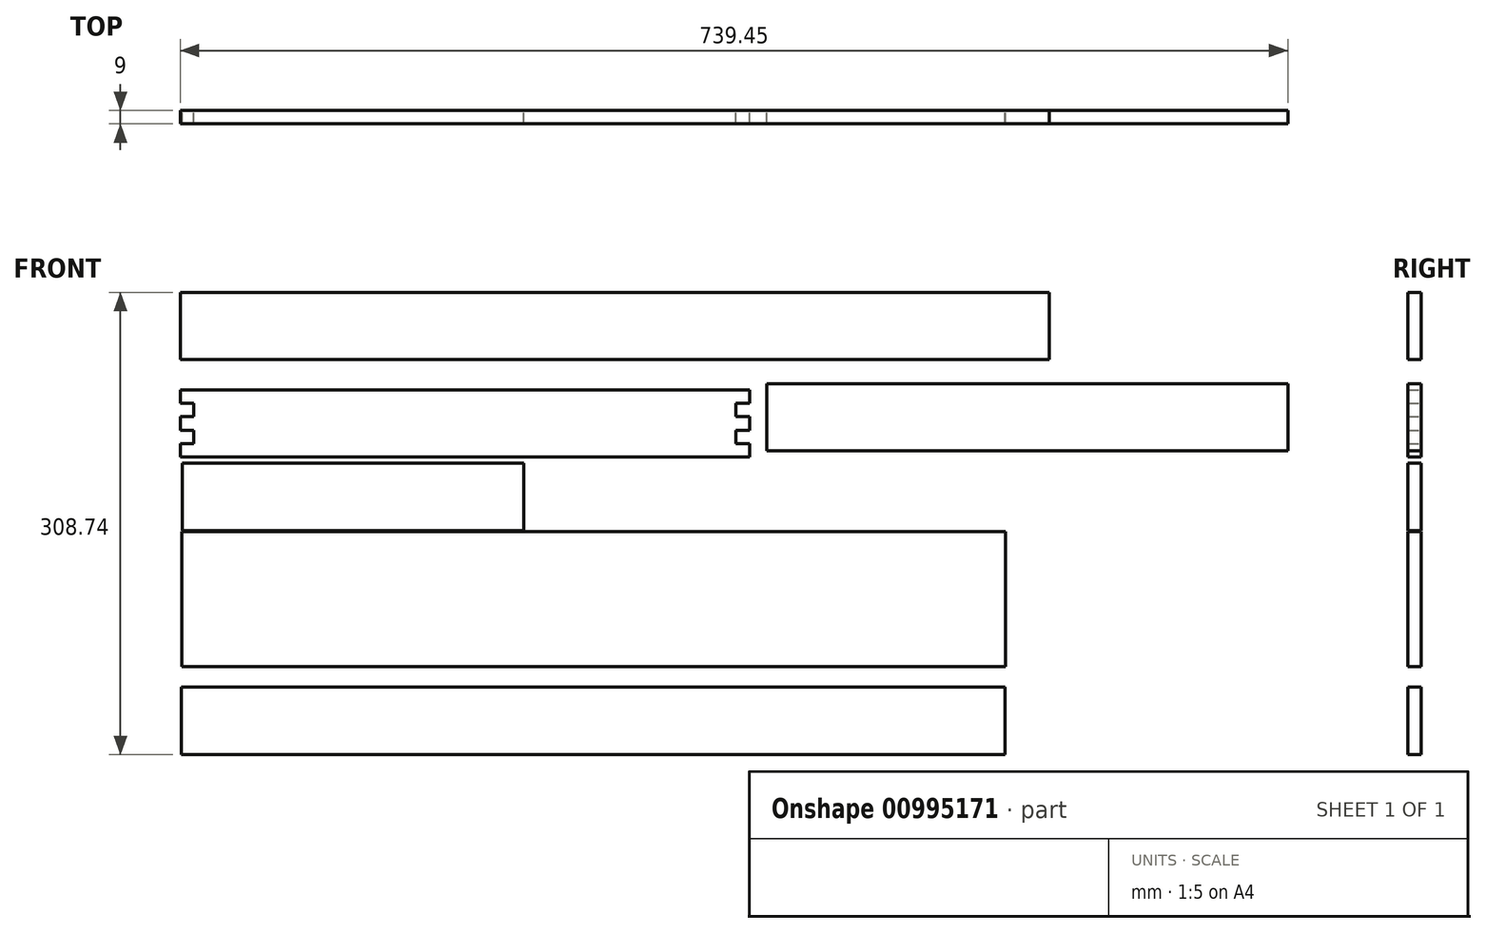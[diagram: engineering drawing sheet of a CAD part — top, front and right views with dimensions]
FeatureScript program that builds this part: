
annotation { "Feature Type Name" : "Feature", "Feature Type Description" : "" }
export const myFeature = defineFeature(function(context is Context, id is Id, definition is map)
    precondition{}
    {
        {
            var Q0;
            Q0=qCreatedBy(makeId("Front.planeOp"),FACE);
            var sketch = newSketch(context, id + "F0", { "sketchPlane" : qUnion([Q0])});
            skLineSegment(sketch, "E0.bottom", {"start": v(-581.65, 301.64) * mm, "end": v(-1.65, 301.64) * mm});
            skLineSegment(sketch, "E0.top", {"start": v(-581.65, 256.64) * mm, "end": v(-1.65, 256.64) * mm});
            skLineSegment(sketch, "E0.left", {"start": v(-581.65, 301.64) * mm, "end": v(-581.65, 256.64) * mm});
            skLineSegment(sketch, "E0.right", {"start": v(-1.65, 301.64) * mm, "end": v(-1.65, 256.64) * mm});
            skSolve(sketch);
        }
        {
            var Q0;
            Q0 = qSketchRegion(id + "F0", true);
            extrude(context, id + "F1", {"entities" : qUnion([Q0]), "depth" : 9 * mm, "offsetDistance" : 25 * mm});
        }
        {
            var Q0;
            Q0=qCreatedBy(makeId("Front.planeOp"),FACE);
            var sketch = newSketch(context, id + "F2", { "sketchPlane" : qUnion([Q0])});
            skLineSegment(sketch, "E1.bottom", {"start": v(-581.64, 236.6) * mm, "end": v(-201.64, 236.6) * mm});
            skLineSegment(sketch, "E1.top", {"start": v(-572.64, 191.6) * mm, "end": v(-201.64, 191.6) * mm});
            skLineSegment(sketch, "E1.left", {"start": v(-581.64, 236.6) * mm, "end": v(-581.64, 227.6) * mm});
            skLineSegment(sketch, "E1.right", {"start": v(-201.64, 236.6) * mm, "end": v(-201.64, 227.6) * mm});
            skLineSegment(sketch, "E2", {"start": v(-572.64, 227.6) * mm, "end": v(-572.64, 218.6) * mm});
            skLineSegment(sketch, "E3", {"start": v(-581.64, 236.6) * mm, "end": v(-572.64, 236.6) * mm});
            skLineSegment(sketch, "E4.0.1.0", {"start": v(-581.64, 227.6) * mm, "end": v(-572.64, 227.6) * mm});
            skLineSegment(sketch, "E4.0.2.0", {"start": v(-581.64, 218.6) * mm, "end": v(-572.64, 218.6) * mm});
            skLineSegment(sketch, "E4.0.3.0", {"start": v(-581.64, 209.6) * mm, "end": v(-572.64, 209.6) * mm});
            skLineSegment(sketch, "E4.0.4.0", {"start": v(-581.64, 200.6) * mm, "end": v(-572.64, 200.6) * mm});
            skLineSegment(sketch, "E4.direction1", {"start": v(-581.64, 236.6) * mm, "end": v(-556.64, 236.6) * mm, "construction": true});
            skLineSegment(sketch, "E4.direction2", {"start": v(-581.64, 236.6) * mm, "end": v(-581.64, 227.6) * mm, "construction": true});
            skLineSegment(sketch, "E5.trimOffspring", {"start": v(-581.64, 218.6) * mm, "end": v(-581.64, 209.6) * mm});
            skLineSegment(sketch, "E6.trimOffspring", {"start": v(-581.64, 200.6) * mm, "end": v(-581.64, 191.6) * mm});
            skLineSegment(sketch, "E7.trimOffspring", {"start": v(-581.64, 182.6) * mm, "end": v(-581.64, 173.6) * mm});
            skLineSegment(sketch, "E8", {"start": v(-210.64, 236.6) * mm, "end": v(-210.64, 218.6) * mm});
            skLineSegment(sketch, "E9", {"start": v(-581.64, 164.6) * mm, "end": v(-581.64, 155.6) * mm});
            skLineSegment(sketch, "E10", {"start": v(-210.64, 236.6) * mm, "end": v(-201.64, 236.6) * mm});
            skLineSegment(sketch, "E11.0.1.0", {"start": v(-210.64, 227.6) * mm, "end": v(-201.64, 227.6) * mm});
            skLineSegment(sketch, "E11.0.2.0", {"start": v(-210.64, 218.6) * mm, "end": v(-201.64, 218.6) * mm});
            skLineSegment(sketch, "E11.0.3.0", {"start": v(-210.64, 209.6) * mm, "end": v(-201.64, 209.6) * mm});
            skLineSegment(sketch, "E11.0.4.0", {"start": v(-210.64, 200.6) * mm, "end": v(-201.64, 200.6) * mm});
            skLineSegment(sketch, "E11.0.5.0", {"start": v(-210.64, 191.6) * mm, "end": v(-201.64, 191.6) * mm});
            skLineSegment(sketch, "E11.direction1", {"start": v(-210.64, 236.6) * mm, "end": v(-185.64, 236.6) * mm, "construction": true});
            skLineSegment(sketch, "E12.trimOffspring", {"start": v(-201.64, 218.6) * mm, "end": v(-201.64, 209.6) * mm});
            skLineSegment(sketch, "E13.trimOffspring", {"start": v(-201.64, 200.6) * mm, "end": v(-201.64, 191.6) * mm});
            skLineSegment(sketch, "E14.trimOffspring", {"start": v(-201.64, 206.6) * mm, "end": v(-201.64, 201.6) * mm});
            skLineSegment(sketch, "E15.trimOffspring", {"start": v(-201.64, 196.6) * mm, "end": v(-201.64, 191.6) * mm});
            skLineSegment(sketch, "E16.0.0.5", {"start": v(-581.64, 191.6) * mm, "end": v(-572.64, 191.6) * mm});
            skLineSegment(sketch, "E17.trimOffspring", {"start": v(-572.64, 209.6) * mm, "end": v(-572.64, 200.6) * mm});
            skLineSegment(sketch, "E18.trimOffspring", {"start": v(-210.64, 209.6) * mm, "end": v(-210.64, 200.6) * mm});
            skSolve(sketch);
        }
        {
            var Q0;
            Q0 = qSketchRegion(id + "F2", true);
            extrude(context, id + "F3", {"entities" : qUnion([Q0]), "depth" : 9 * mm, "offsetDistance" : 25 * mm});
        }
        {
            var Q0;
            Q0=qCreatedBy(makeId("Front.planeOp"),FACE);
            var sketch = newSketch(context, id + "F4", { "sketchPlane" : qUnion([Q0])});
            skLineSegment(sketch, "E19.bottom", {"start": v(-190.2, 240.7) * mm, "end": v(157.8, 240.7) * mm});
            skLineSegment(sketch, "E19.top", {"start": v(-190.2, 195.7) * mm, "end": v(157.8, 195.7) * mm});
            skLineSegment(sketch, "E19.left", {"start": v(-190.2, 240.7) * mm, "end": v(-190.2, 195.7) * mm});
            skLineSegment(sketch, "E19.right", {"start": v(157.8, 240.7) * mm, "end": v(157.8, 195.7) * mm});
            skSolve(sketch);
        }
        {
            var Q0;
            Q0 = qSketchRegion(id + "F4", true);
            extrude(context, id + "F5", {"entities" : qUnion([Q0]), "depth" : 9 * mm, "offsetDistance" : 25 * mm});
        }
        {
            var Q0;
            Q0=qCreatedBy(makeId("Front.planeOp"),FACE);
            var sketch = newSketch(context, id + "F6", { "sketchPlane" : qUnion([Q0])});
            skLineSegment(sketch, "E20.bottom", {"start": v(-580.33, 187.47) * mm, "end": v(-352.33, 187.47) * mm});
            skLineSegment(sketch, "E20.top", {"start": v(-580.33, 142.47) * mm, "end": v(-352.33, 142.47) * mm});
            skLineSegment(sketch, "E20.left", {"start": v(-580.33, 187.47) * mm, "end": v(-580.33, 142.47) * mm});
            skLineSegment(sketch, "E20.right", {"start": v(-352.33, 187.47) * mm, "end": v(-352.33, 142.47) * mm});
            skSolve(sketch);
        }
        {
            var Q0;
            Q0=makeQuery(id+"F6.imprint","IMPRINT",FACE,{"disambiguationData":[TD([[makeQuery(id+"F6.imprint","IMPRINT",EDGE,{"derivedFrom":sQuery(id+"F6.wireOp",EDGE,"E20.bottom")}),-1.0]])]});
            extrude(context, id + "F7", {"entities" : qUnion([Q0]), "depth" : 9 * mm, "offsetDistance" : 25 * mm});
        }
        {
            var Q0;
            Q0=qCreatedBy(makeId("Front.planeOp"),FACE);
            var sketch = newSketch(context, id + "F8", { "sketchPlane" : qUnion([Q0])});
            skLineSegment(sketch, "E21.bottom", {"start": v(-580.58, 141.8) * mm, "end": v(-30.58, 141.8) * mm});
            skLineSegment(sketch, "E21.top", {"start": v(-580.58, 51.8) * mm, "end": v(-30.58, 51.8) * mm});
            skLineSegment(sketch, "E21.left", {"start": v(-580.58, 141.8) * mm, "end": v(-580.58, 51.8) * mm});
            skLineSegment(sketch, "E21.right", {"start": v(-30.58, 141.8) * mm, "end": v(-30.58, 51.8) * mm});
            skSolve(sketch);
        }
        {
            var Q0;
            Q0 = qSketchRegion(id + "F8", true);
            extrude(context, id + "F9", {"entities" : qUnion([Q0]), "depth" : 9 * mm, "offsetDistance" : 25 * mm});
        }
        {
            var Q0;
            Q0=qCreatedBy(makeId("Front.planeOp"),FACE);
            var sketch = newSketch(context, id + "F10", { "sketchPlane" : qUnion([Q0])});
            skLineSegment(sketch, "E22.bottom", {"start": v(-581.04, 37.9) * mm, "end": v(-31.04, 37.9) * mm});
            skLineSegment(sketch, "E22.top", {"start": v(-581.04, -7.1) * mm, "end": v(-31.04, -7.1) * mm});
            skLineSegment(sketch, "E22.left", {"start": v(-581.04, 37.9) * mm, "end": v(-581.04, -7.1) * mm});
            skLineSegment(sketch, "E22.right", {"start": v(-31.04, 37.9) * mm, "end": v(-31.04, -7.1) * mm});
            skSolve(sketch);
        }
        {
            var Q0;
            Q0=makeQuery(id+"F10.imprint","IMPRINT",FACE,{"disambiguationData":[TD([[makeQuery(id+"F10.imprint","IMPRINT",EDGE,{"derivedFrom":sQuery(id+"F10.wireOp",EDGE,"E22.bottom")}),-1.0]])]});
            extrude(context, id + "F11", {"entities" : qUnion([Q0]), "depth" : 9 * mm, "offsetDistance" : 25 * mm});
        }
    });
